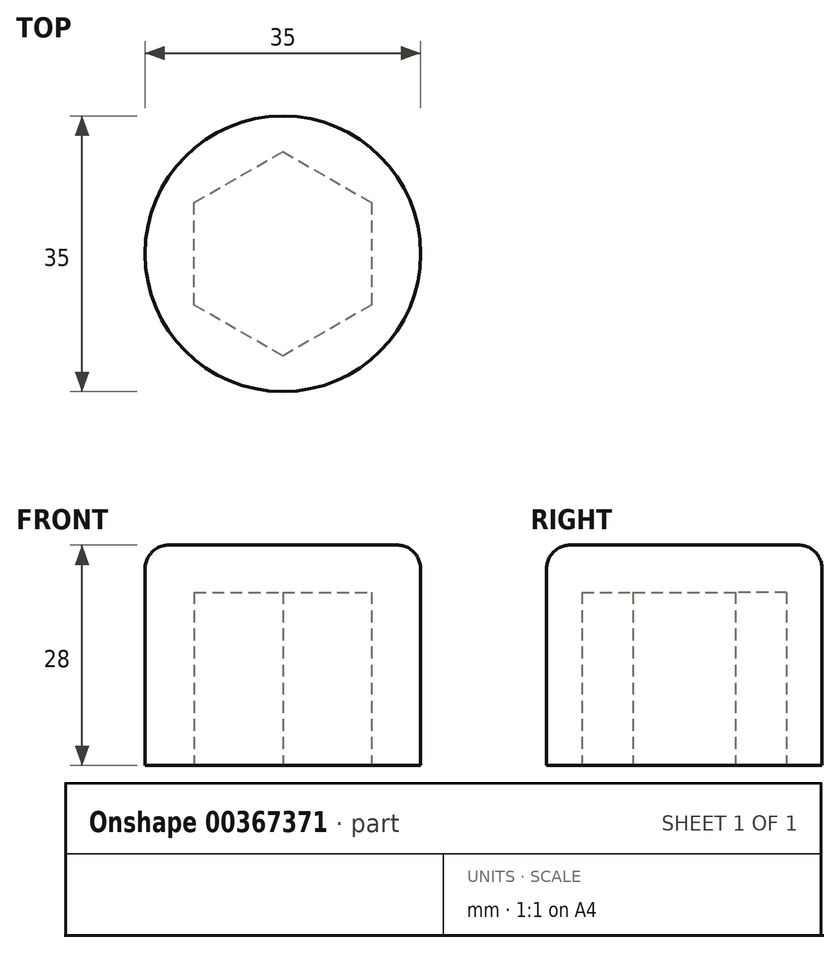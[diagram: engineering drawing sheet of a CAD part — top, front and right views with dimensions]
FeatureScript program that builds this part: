
annotation { "Feature Type Name" : "Feature", "Feature Type Description" : "" }
export const myFeature = defineFeature(function(context is Context, id is Id, definition is map)
    precondition{}
    {
        {
            var Q0;
            Q0=qCreatedBy(makeId("Top.planeOp"),FACE);
            var sketch = newSketch(context, id + "F0", { "sketchPlane" : qUnion([Q0])});
            skCircle(sketch, "E0.cCircle", {"center": v(0, 0) * mm, "radius": 11.25 * mm, "construction": true});
            skLineSegment(sketch, "E0.0", {"start": v(0, 13) * mm, "end": v(11.25, 6.5) * mm});
            skLineSegment(sketch, "E0.1", {"start": v(11.25, 6.5) * mm, "end": v(11.25, -6.5) * mm});
            skLineSegment(sketch, "E0.2", {"start": v(11.25, -6.5) * mm, "end": v(0, -13) * mm});
            skLineSegment(sketch, "E0.3", {"start": v(0, -13) * mm, "end": v(-11.25, -6.5) * mm});
            skLineSegment(sketch, "E0.4", {"start": v(-11.25, -6.5) * mm, "end": v(-11.25, 6.5) * mm});
            skLineSegment(sketch, "E0.5", {"start": v(-11.25, 6.5) * mm, "end": v(0, 13) * mm});
            skPoint(sketch, "E0.0.midPoint", {"position": v(5.62, 9.74) * mm});
            skCircle(sketch, "E1", {"center": v(0, 0) * mm, "radius": 17.5 * mm});
            skSolve(sketch);
        }
        {
            var Q0;
            Q0=makeQuery(id+"F0.imprint","IMPRINT",FACE,{"disambiguationData":[TD([[makeQuery(id+"F0.imprint","IMPRINT",EDGE,{"derivedFrom":sQuery(id+"F0.wireOp",EDGE,"E0.0")}),-1.0]])]});
            var Q1;
            Q1=makeQuery(id+"F0.imprint","IMPRINT",FACE,{"disambiguationData":[TD([[makeQuery(id+"F0.imprint","IMPRINT",EDGE,{"derivedFrom":sQuery(id+"F0.wireOp",EDGE,"E0.0")}),1.0]])]});
            extrude(context, id + "F1", {"entities" : qUnion([Q0, Q1]), "depth" : 28 * mm});
        }
        {
            var Q0;
            Q0=makeQuery(id+"F0.imprint","IMPRINT",FACE,{"disambiguationData":[TD([[makeQuery(id+"F0.imprint","IMPRINT",EDGE,{"derivedFrom":sQuery(id+"F0.wireOp",EDGE,"E0.0")}),-1.0]])]});
            extrude(context, id + "F2", {"entities" : qUnion([Q0]), "operationType" : NewBodyOperationType.REMOVE, "depth" : 22 * mm});
        }
        {
            var Q0;
            Q0=makeQuery(id+"F1.opExtrude","CAP_EDGE",EDGE,{"disambiguationData":[OSD([sQuery(id+"F0.wireOp",EDGE,"E1")])],"isStart":false});
            fillet(context, id + "F3", {"entities" : qUnion([Q0]), "radius" : 3 * mm, "tangentPropagation" : true, "allowEdgeOverflow" : false});
        }
    });
